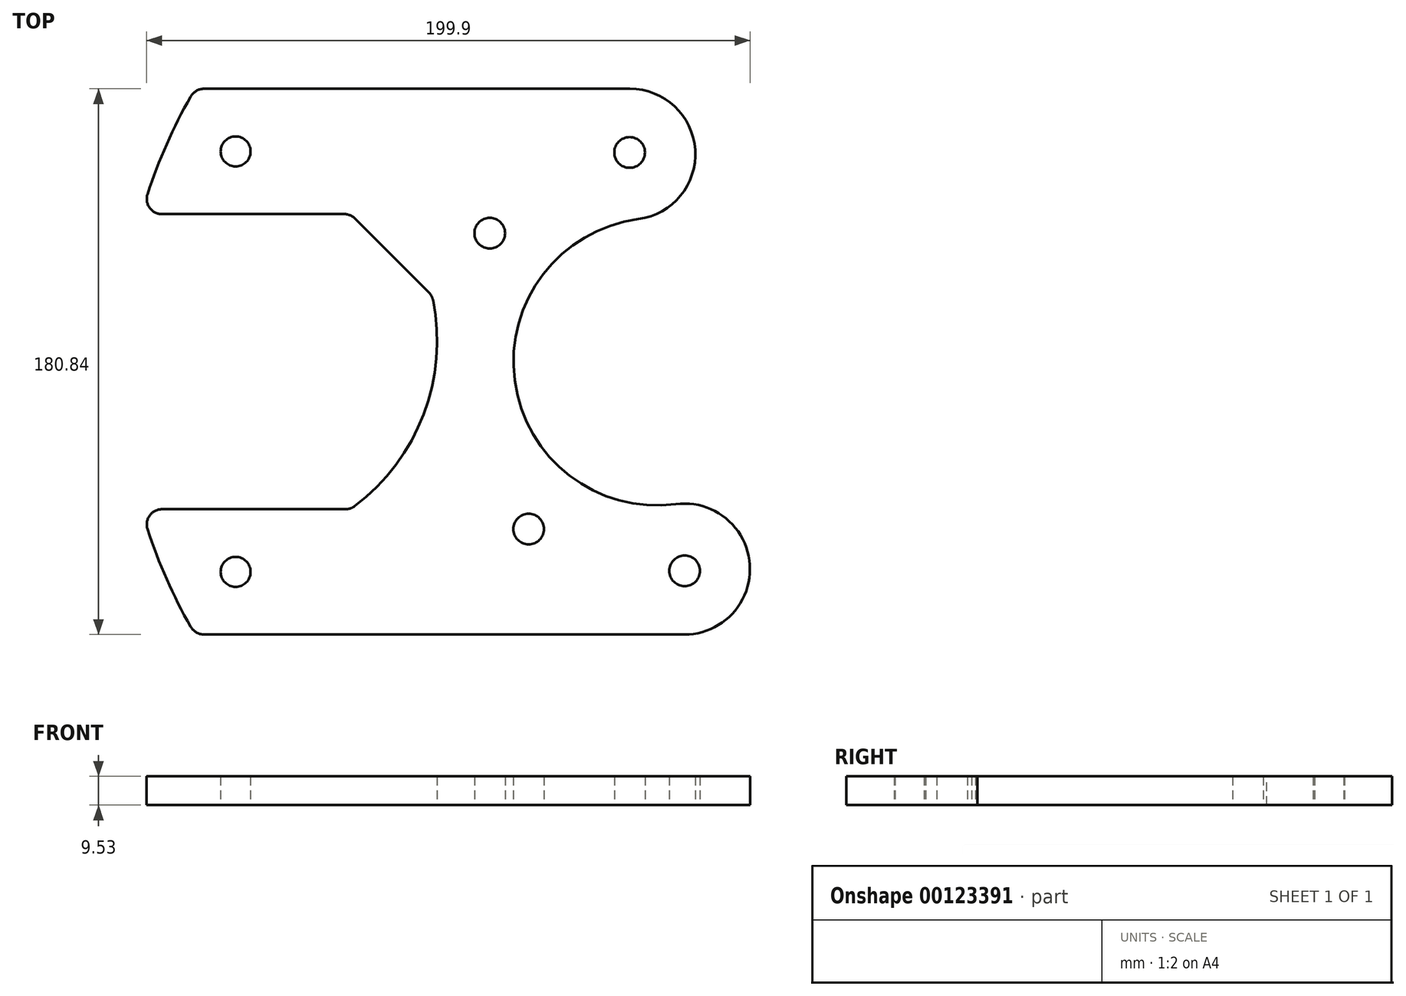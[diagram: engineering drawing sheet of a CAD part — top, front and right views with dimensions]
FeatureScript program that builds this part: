
annotation { "Feature Type Name" : "Feature", "Feature Type Description" : "" }
export const myFeature = defineFeature(function(context is Context, id is Id, definition is map)
    precondition{}
    {
        {
            var Q0;
            Q0=qCreatedBy(makeId("Top.planeOp"),FACE);
            var sketch = newSketch(context, id + "F0", { "sketchPlane" : qUnion([Q0])});
            skArc(sketch, "E0", {"start": v(-48.78, 47.22) * mm, "mid": v(-89.79, -6.22) * mm, "end": v(-36.35, -47.22) * mm});
            skCircle(sketch, "E1", {"center": v(-42.57, 0) * mm, "radius": 69.93 * mm, "construction": true});
            skLineSegment(sketch, "E2", {"start": v(-144.17, 48.9) * mm, "end": v(-213.51, 48.9) * mm});
            skLineSegment(sketch, "E3", {"start": v(-144.17, -48.9) * mm, "end": v(-213.51, -48.9) * mm});
            skCircle(sketch, "E4", {"center": v(-182.27, 69.66) * mm, "radius": 4.96 * mm});
            skCircle(sketch, "E5", {"center": v(-182.27, -69.66) * mm, "radius": 4.96 * mm});
            skLineSegment(sketch, "E6", {"start": v(-281.65, 0) * mm, "end": v(212.8, 0) * mm, "construction": true});
            skLineSegment(sketch, "E7", {"start": v(-182.27, 69.66) * mm, "end": v(-182.27, -69.66) * mm, "construction": true});
            skPoint(sketch, "E8", {"position": v(-182.27, 0) * mm});
            skCircle(sketch, "E9", {"center": v(-85.14, -55.48) * mm, "radius": 5.08 * mm});
            skCircle(sketch, "E10", {"center": v(-33.44, -69.33) * mm, "radius": 5.08 * mm});
            skCircle(sketch, "E11", {"center": v(12.9, -42.57) * mm, "radius": 5.08 * mm, "construction": true});
            skCircle(sketch, "E12", {"center": v(0, 55.48) * mm, "radius": 5.08 * mm, "construction": true});
            skCircle(sketch, "E13", {"center": v(-51.7, 69.33) * mm, "radius": 5.08 * mm});
            skCircle(sketch, "E14", {"center": v(-98.04, 42.57) * mm, "radius": 5.08 * mm});
            skLineSegment(sketch, "E15", {"start": v(-85.14, -55.48) * mm, "end": v(-98.04, 42.57) * mm, "construction": true});
            skLineSegment(sketch, "E16", {"start": v(-33.44, -69.33) * mm, "end": v(-51.7, 69.33) * mm, "construction": true});
            skLineSegment(sketch, "E17", {"start": v(12.9, -42.57) * mm, "end": v(0, 55.48) * mm, "construction": true});
            skLineSegment(sketch, "E18", {"start": v(-85.14, -55.48) * mm, "end": v(0, 55.48) * mm, "construction": true});
            skLineSegment(sketch, "E19", {"start": v(12.9, -42.57) * mm, "end": v(-98.04, 42.57) * mm, "construction": true});
            skLineSegment(sketch, "E20", {"start": v(-144.17, 48.9) * mm, "end": v(-117.17, 21.9) * mm});
            skArc(sketch, "E21", {"start": v(-144.17, -48.9) * mm, "mid": v(-120, -17.57) * mm, "end": v(-117.17, 21.9) * mm});
            skArc(sketch, "E22", {"start": v(-182.27, 90.42) * mm, "mid": v(-203.03, 69.66) * mm, "end": v(-182.27, 48.9) * mm, "construction": true});
            skArc(sketch, "E23", {"start": v(-182.27, -48.9) * mm, "mid": v(-203.03, -69.66) * mm, "end": v(-182.27, -90.42) * mm, "construction": true});
            skLineSegment(sketch, "E24", {"start": v(-195.66, -90.42) * mm, "end": v(-33.52, -90.42) * mm});
            skLineSegment(sketch, "E25", {"start": v(-182.27, 90.42) * mm, "end": v(-51.62, 90.42) * mm});
            skCircle(sketch, "E26", {"center": v(-42.57, 0) * mm, "radius": 147.32 * mm, "construction": true});
            skLineSegment(sketch, "E27", {"start": v(-177.95, -67.91) * mm, "end": v(-174.15, -66.24) * mm, "construction": true});
            skCircle(sketch, "E28", {"center": v(-182.27, -69.66) * mm, "radius": 4.66 * mm, "construction": true});
            skCircle(sketch, "E29", {"center": v(-182.27, 69.66) * mm, "radius": 4.66 * mm, "construction": true});
            skLineSegment(sketch, "E30", {"start": v(-182.27, 90.42) * mm, "end": v(-195.66, 90.42) * mm});
            skArc(sketch, "E31", {"start": v(-195.66, 90.42) * mm, "mid": v(-205.91, 70.23) * mm, "end": v(-213.51, 48.9) * mm});
            skArc(sketch, "E32.trimOffspring", {"start": v(-213.51, -48.9) * mm, "mid": v(-205.91, -70.23) * mm, "end": v(-195.66, -90.42) * mm});
            skArc(sketch, "E33", {"start": v(-48.78, 47.22) * mm, "mid": v(-29.97, 70.15) * mm, "end": v(-51.62, 90.42) * mm});
            skArc(sketch, "E34", {"start": v(-33.52, -90.42) * mm, "mid": v(-11.87, -67.3) * mm, "end": v(-36.35, -47.22) * mm});
            skSolve(sketch);
        }
        {
            var Q0;
            Q0=qSketchRegion(id+"F0",true);
            extrude(context, id + "F1", {"entities" : qUnion([Q0]), "depth" : 9.52 * mm});
        }
        {
            var Q0;
            Q0=makeQuery(id+"F1.opExtrude","SWEPT_EDGE",EDGE,{"disambiguationData":[OSD([sQuery(id+"F0.wireOp",EDGE,"E2"),sQuery(id+"F0.wireOp",EDGE,"E20")])]});
            var Q1;
            Q1=makeQuery(id+"F1.opExtrude","SWEPT_EDGE",EDGE,{"disambiguationData":[OSD([sQuery(id+"F0.wireOp",EDGE,"E20"),sQuery(id+"F0.wireOp",EDGE,"E21")])]});
            var Q2;
            Q2=makeQuery(id+"F1.opExtrude","SWEPT_EDGE",EDGE,{"disambiguationData":[OSD([sQuery(id+"F0.wireOp",EDGE,"E3"),sQuery(id+"F0.wireOp",EDGE,"E21")])]});
            var Q3;
            Q3=makeQuery(id+"F1.opExtrude","SWEPT_EDGE",EDGE,{"disambiguationData":[OSD([sQuery(id+"F0.wireOp",EDGE,"E3"),sQuery(id+"F0.wireOp",EDGE,"E32.trimOffspring")])]});
            var Q4;
            Q4=makeQuery(id+"F1.opExtrude","SWEPT_EDGE",EDGE,{"disambiguationData":[OSD([sQuery(id+"F0.wireOp",EDGE,"E24"),sQuery(id+"F0.wireOp",EDGE,"E32.trimOffspring")])]});
            var Q5;
            Q5=makeQuery(id+"F1.opExtrude","SWEPT_EDGE",EDGE,{"disambiguationData":[OSD([sQuery(id+"F0.wireOp",EDGE,"E2"),sQuery(id+"F0.wireOp",EDGE,"E31")])]});
            var Q6;
            Q6=makeQuery(id+"F1.opExtrude","SWEPT_EDGE",EDGE,{"disambiguationData":[OSD([sQuery(id+"F0.wireOp",EDGE,"E30"),sQuery(id+"F0.wireOp",EDGE,"E31")])]});
            fillet(context, id + "F2", {"entities" : qUnion([Q0, Q1, Q2, Q3, Q4, Q5, Q6]), "radius" : 5.08 * mm, "tangentPropagation" : true, "allowEdgeOverflow" : false});
        }
    });
